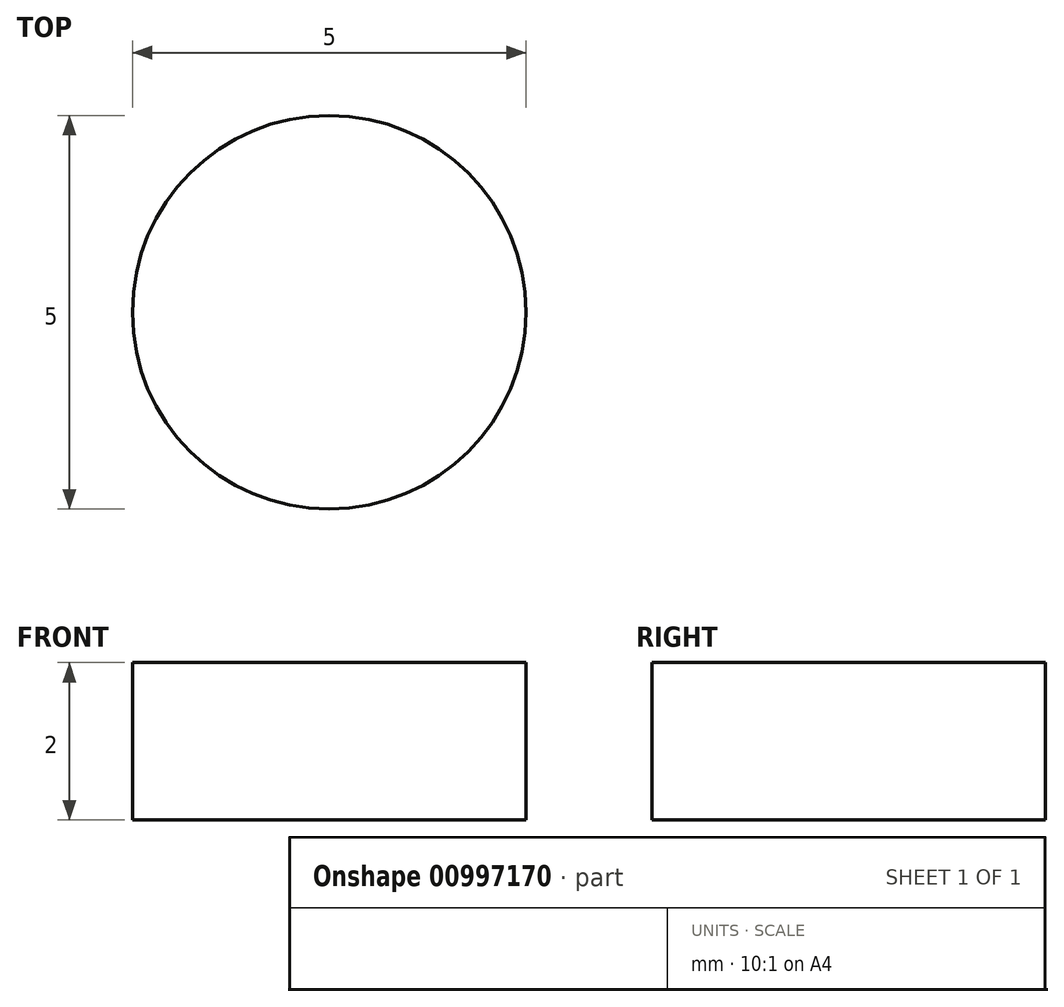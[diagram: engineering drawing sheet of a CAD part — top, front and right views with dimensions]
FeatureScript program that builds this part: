
annotation { "Feature Type Name" : "Feature", "Feature Type Description" : "" }
export const myFeature = defineFeature(function(context is Context, id is Id, definition is map)
    precondition{}
    {
        {
            var Q0;
            Q0=qCreatedBy(makeId("Top.planeOp"),FACE);
            var sketch = newSketch(context, id + "F0", { "sketchPlane" : qUnion([Q0])});
            skCircle(sketch, "E0", {"center": v(0, 0) * mm, "radius": 2.5 * mm});
            skSolve(sketch);
        }
        {
            var Q0;
            Q0 = qSketchRegion(id + "F0", true);
            extrude(context, id + "F1", {"entities" : qUnion([Q0]), "depth" : 2 * mm, "offsetDistance" : 25 * mm});
        }
    });
